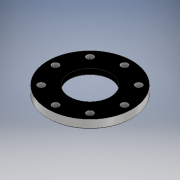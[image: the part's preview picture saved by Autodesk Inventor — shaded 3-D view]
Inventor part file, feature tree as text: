
AUTODESK INVENTOR PART (.ipt)
format: ipt  version: 2023 (Build 270158000, 158)  size: 412,672 bytes
history: native  units: mm
features: other x3, extrude x3, sketch x3
ambient origin geometry x8: Origin, YZ Plane, XZ Plane, XY Plane, X Axis, Y Axis, Z Axis, Center Point
bodies: Body1 (feature_tree)
feature tree (9):
  other  "ソリッド1"
  other  "作業平面1"
  extrude  "押し出し1"  Depth=0.5mm
  extrude  "押し出し2"  Depth=10.0mm TaperAngle=0.0deg
  extrude  "押し出し4"  Depth=15.0mm
  sketch  "スケッチ1"
  sketch  "スケッチ2"
  sketch  "スケッチ4"
  other  "X-430_IDLE_10:1"
